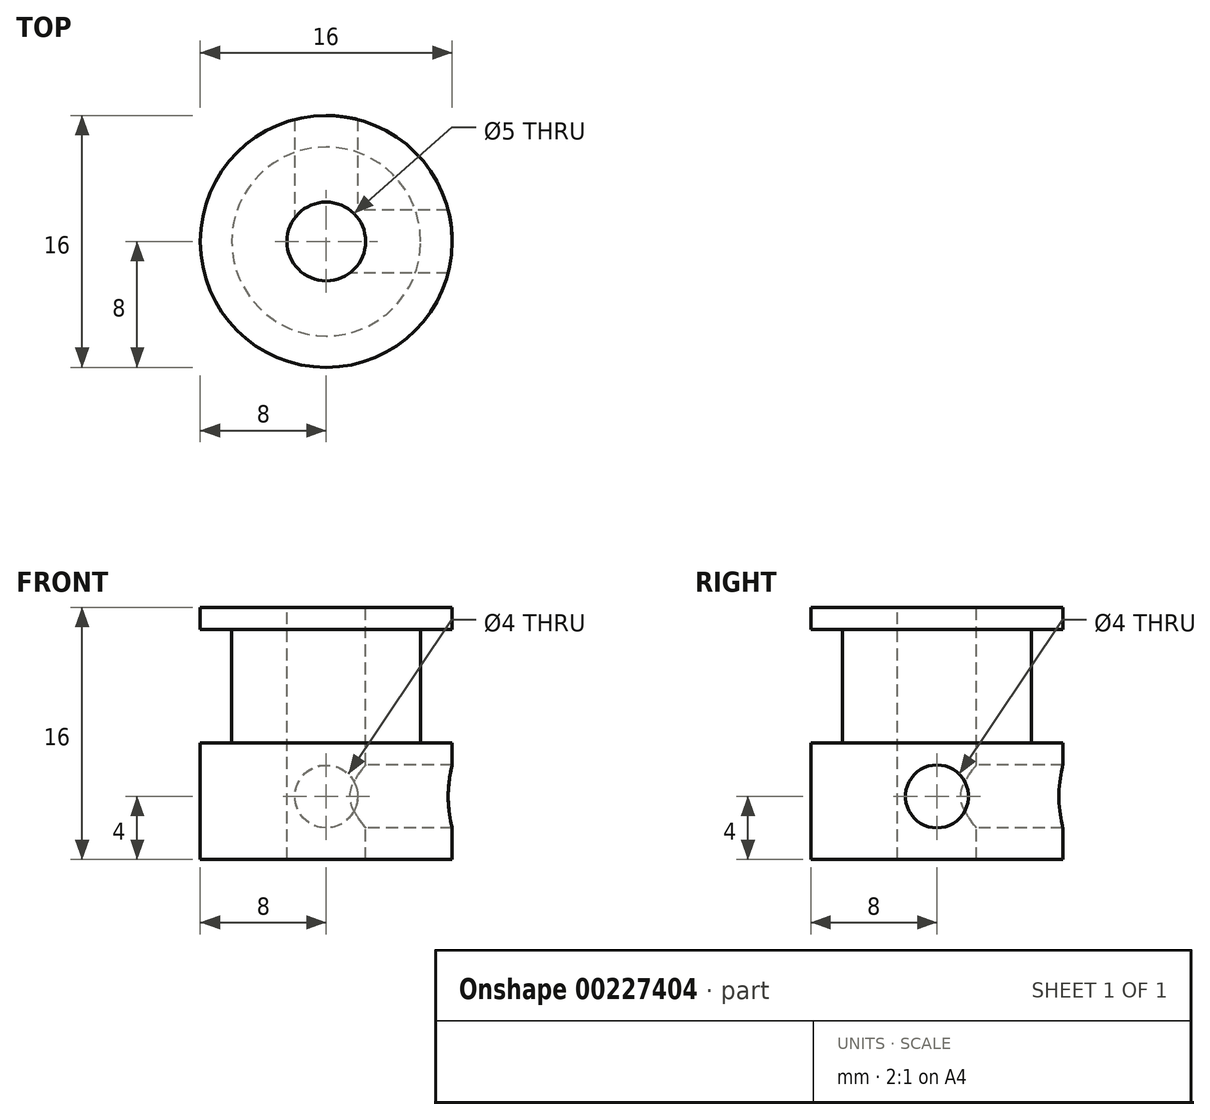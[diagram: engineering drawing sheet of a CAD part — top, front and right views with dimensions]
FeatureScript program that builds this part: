
annotation { "Feature Type Name" : "Feature", "Feature Type Description" : "" }
export const myFeature = defineFeature(function(context is Context, id is Id, definition is map)
    precondition{}
    {
        {
            var Q0;
            Q0=qCreatedBy(makeId("Front.planeOp"),FACE);
            var sketch = newSketch(context, id + "F0", { "sketchPlane" : qUnion([Q0])});
            skLineSegment(sketch, "E0", {"start": v(0, 26.54) * mm, "end": v(0, -21.41) * mm, "construction": true});
            skLineSegment(sketch, "E1", {"start": v(0, 8.6) * mm, "end": v(8, 8.6) * mm});
            skLineSegment(sketch, "E2", {"start": v(8, 8.6) * mm, "end": v(8, 7.2) * mm});
            skLineSegment(sketch, "E3", {"start": v(8, 7.2) * mm, "end": v(6, 7.2) * mm});
            skLineSegment(sketch, "E4", {"start": v(6, 7.2) * mm, "end": v(6, 0) * mm});
            skLineSegment(sketch, "E5", {"start": v(6, 0) * mm, "end": v(8, 0) * mm});
            skLineSegment(sketch, "E6", {"start": v(8, 0) * mm, "end": v(8, -7.4) * mm});
            skLineSegment(sketch, "E7", {"start": v(8, -7.4) * mm, "end": v(0, -7.4) * mm});
            skLineSegment(sketch, "E8", {"start": v(2.5, 8.6) * mm, "end": v(2.5, -7.4) * mm});
            skSolve(sketch);
        }
        {
            var Q0;
            {var subQ0=sQuery(id+"F0.wireOp",EDGE,"E2");Q0=makeQuery(id+"F0.imprint","IMPRINT",FACE,{"disambiguationData":[TD([[makeQuery(id+"F0.imprint","IMPRINT",EDGE,{"derivedFrom":subQ0}),-1.0]])]});}
            var Q1;
            Q1=sQuery(id+"F0.wireOp",EDGE,"E0");
            revolve(context, id + "F1", {"entities" : qUnion([Q0]), "axis" : qUnion([Q1]), "revolveType" : RevolveType.FULL});
        }
        {
            var Q0;
            Q0=qCreatedBy(makeId("Right.planeOp"),FACE);
            var sketch = newSketch(context, id + "F2", { "sketchPlane" : qUnion([Q0])});
            skCircle(sketch, "E9", {"center": v(0, -3.4) * mm, "radius": 2 * mm});
            skSolve(sketch);
        }
        {
            var Q0;
            Q0=makeQuery(id+"F2.imprint","IMPRINT",FACE,{"disambiguationData":[TD([[makeQuery(id+"F2.imprint","IMPRINT",EDGE,{"derivedFrom":sQuery(id+"F2.wireOp",EDGE,"E9")}),1.0]])]});
            extrude(context, id + "F3", {"entities" : qUnion([Q0]), "operationType" : NewBodyOperationType.REMOVE, "depth" : 25 * mm});
        }
        {
            var Q0;
            Q0=qCreatedBy(makeId("Front.planeOp"),FACE);
            var sketch = newSketch(context, id + "F4", { "sketchPlane" : qUnion([Q0])});
            skCircle(sketch, "E10", {"center": v(0, -3.4) * mm, "radius": 2 * mm});
            skSolve(sketch);
        }
        {
            var Q0;
            Q0=makeQuery(id+"F4.imprint","IMPRINT",FACE,{"disambiguationData":[TD([[makeQuery(id+"F4.imprint","IMPRINT",EDGE,{"derivedFrom":sQuery(id+"F4.wireOp",EDGE,"E10")}),1.0]])]});
            extrude(context, id + "F5", {"entities" : qUnion([Q0]), "operationType" : NewBodyOperationType.REMOVE, "oppositeDirection" : true, "depth" : 25 * mm});
        }
    });
